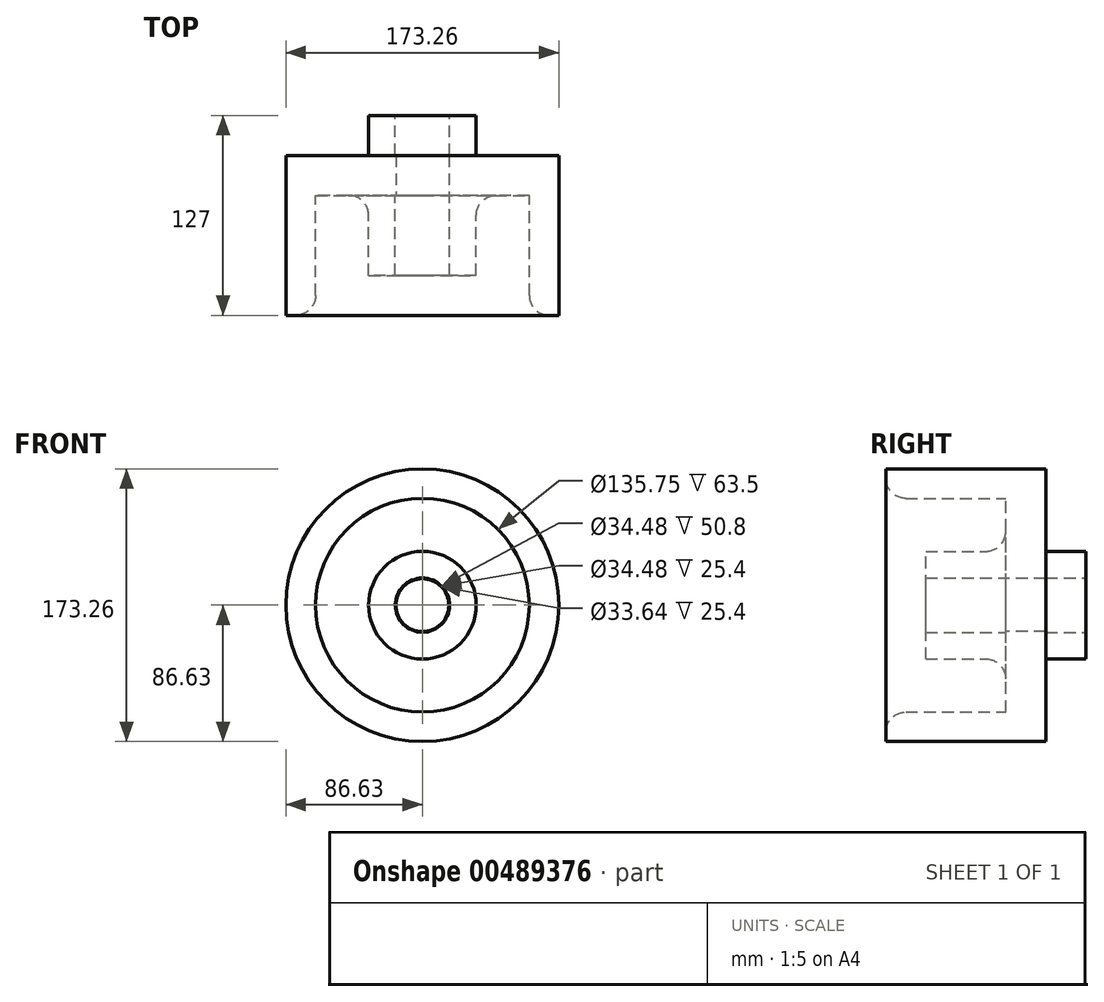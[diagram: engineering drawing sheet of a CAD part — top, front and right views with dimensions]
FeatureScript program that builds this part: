
annotation { "Feature Type Name" : "Feature", "Feature Type Description" : "" }
export const myFeature = defineFeature(function(context is Context, id is Id, definition is map)
    precondition{}
    {
        {
            var Q0;
            Q0=qCreatedBy(makeId("Front.planeOp"),FACE);
            var sketch = newSketch(context, id + "F0", { "sketchPlane" : qUnion([Q0])});
            skCircle(sketch, "E0", {"center": v(0, 0) * mm, "radius": 86.63 * mm});
            skSolve(sketch);
        }
        {
            var Q0;
            Q0=makeQuery(id+"F0.imprint","IMPRINT",FACE,{"disambiguationData":[TD([[makeQuery(id+"F0.imprint","IMPRINT",EDGE,{"derivedFrom":sQuery(id+"F0.wireOp",EDGE,"E0")}),1.0]])]});
            extrude(context, id + "F1", {"entities" : qUnion([Q0]), "depth" : 25.4 * mm});
        }
        {
            var Q0;
            Q0=makeQuery(id+"F1.opExtrude","CAP_FACE",FACE,{"disambiguationData":[OSD([sQuery(id+"F0.wireOp",EDGE,"E0")])],"isStart":false});
            var sketch = newSketch(context, id + "F2", { "sketchPlane" : qUnion([Q0])});
            skCircle(sketch, "E1", {"center": v(0, 0) * mm, "radius": 87.32 * mm});
            skCircle(sketch, "E2", {"center": v(0, 0) * mm, "radius": 67.88 * mm});
            skSolve(sketch);
        }
        {
            var Q0;
            Q0=makeQuery(id+"F2.imprint","IMPRINT",FACE,{"disambiguationData":[TD([[makeQuery(id+"F2.imprint","IMPRINT",EDGE,{"derivedFrom":sQuery(id+"F2.wireOp",EDGE,"E2")}),-1.0]])]});
            extrude(context, id + "F3", {"entities" : qUnion([Q0]), "operationType" : NewBodyOperationType.ADD, "depth" : 76.2 * mm});
        }
        {
            var Q0;
            Q0=makeQuery(id+"F1.opExtrude","CAP_FACE",FACE,{"disambiguationData":[OSD([sQuery(id+"F0.wireOp",EDGE,"E0")])],"isStart":false});
            var sketch = newSketch(context, id + "F4", { "sketchPlane" : qUnion([Q0])});
            skCircle(sketch, "E3", {"center": v(0, 0) * mm, "radius": 34.18 * mm});
            skCircle(sketch, "E4", {"center": v(0, 0) * mm, "radius": 17.24 * mm});
            skSolve(sketch);
        }
        {
            var Q0;
            Q0=makeQuery(id+"F4.imprint","IMPRINT",FACE,{"disambiguationData":[TD([[makeQuery(id+"F4.imprint","IMPRINT",EDGE,{"derivedFrom":sQuery(id+"F4.wireOp",EDGE,"E3")}),1.0]])]});
            extrude(context, id + "F5", {"entities" : qUnion([Q0]), "operationType" : NewBodyOperationType.ADD, "depth" : 50.8 * mm, "hasSecondDirection" : true, "secondDirectionOppositeDirection" : true, "secondDirectionDepth" : 50.8 * mm});
        }
        {
            var Q0;
            Q0=makeQuery(id+"F5.boolean.opBoolean","SPLIT",FACE,{"disambiguationData":[TD([makeQuery(id+"F5.opExtrude","SWEPT_FACE",FACE,{"disambiguationData":[OSD([sQuery(id+"F4.wireOp",EDGE,"E4")])]})])],"derivedFrom":makeQuery(id+"F1.opExtrude","CAP_FACE",FACE,{"disambiguationData":[OSD([sQuery(id+"F0.wireOp",EDGE,"E0")])],"isStart":false})});
            var sketch = newSketch(context, id + "F6", { "sketchPlane" : qUnion([Q0])});
            skCircle(sketch, "E5", {"center": v(0, 0) * mm, "radius": 16.82 * mm});
            skSolve(sketch);
        }
        {
            var Q0;
            Q0=makeQuery(id+"F6.imprint","IMPRINT",FACE,{"disambiguationData":[TD([[makeQuery(id+"F6.imprint","IMPRINT",EDGE,{"derivedFrom":sQuery(id+"F6.wireOp",EDGE,"E5")}),1.0]])]});
            extrude(context, id + "F7", {"entities" : qUnion([Q0]), "operationType" : NewBodyOperationType.REMOVE, "oppositeDirection" : true, "depth" : 50.8 * mm});
        }
        {
            var Q0;
            Q0=makeQuery(id+"F3.opExtrude","CAP_EDGE",EDGE,{"disambiguationData":[OSD([sQuery(id+"F2.wireOp",EDGE,"E2")])],"isStart":false});
            fillet(context, id + "F8", {"entities" : qUnion([Q0]), "radius" : 12.7 * mm, "tangentPropagation" : true, "allowEdgeOverflow" : false});
        }
        {
            var Q0;
            Q0=makeQuery(id+"F3.opExtrude","CAP_EDGE",EDGE,{"disambiguationData":[OSD([sQuery(id+"F2.wireOp",EDGE,"E2")])],"isStart":true});
            var Q1;
            Q1=makeQuery(id+"F5.boolean.opBoolean","INTERSECT",EDGE,{"derivedFrom":[makeQuery(id+"F1.opExtrude","CAP_FACE",FACE,{"disambiguationData":[OSD([sQuery(id+"F0.wireOp",EDGE,"E0")])],"isStart":false}),makeQuery(id+"F5.opExtrude","SWEPT_FACE",FACE,{"disambiguationData":[OSD([sQuery(id+"F4.wireOp",EDGE,"E3")])]})]});
            fillet(context, id + "F9", {"entities" : qUnion([Q0, Q1]), "radius" : 12.7 * mm, "tangentPropagation" : true, "allowEdgeOverflow" : false});
        }
    });
